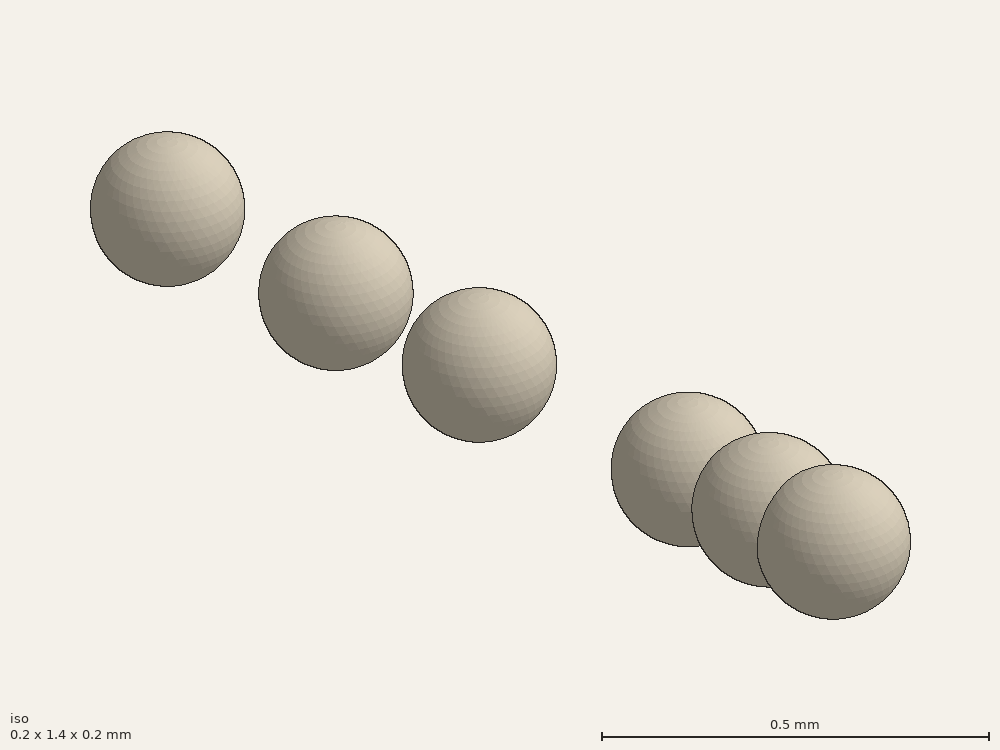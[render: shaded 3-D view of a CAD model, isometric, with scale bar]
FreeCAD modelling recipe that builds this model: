
FCSTD DOCUMENT  (FreeCAD 0.18R14555 (Git shallow))
Label: SIN_COS_TAN
License: All rights reserved
LicenseURL: http://en.wikipedia.org/wiki/All_rights_reserved
objects: Part::Feature×27, App::DocumentObjectGroupPython×7, Part::MultiFuse×6, Part::Part2DObjectPython×5, Part::Compound×4, Sketcher::SketchObject×1, PartDesign::Body×1, Part::Sphere×1
note: 45 computed .brp shape members not serialized (recipe doc carries the construction recipe); baked Part::Feature solids carry a one-line shape summary decoded from their .brp

FEATURE [Sketcher::SketchObject] Sketch
  MapMode = 5
  Support = -> [XY_Plane]
  sketch-geometry (17):
    g0: LineSegment StartX=0 StartY=1 StartZ=0 EndX=0 EndY=0 EndZ=0
    g1: LineSegment StartX=0 StartY=0 StartZ=0 EndX=0.523599 EndY=0 EndZ=0
    g2: LineSegment StartX=0.523599 StartY=0 StartZ=0 EndX=0.523599 EndY=0.5 EndZ=0
    g3: LineSegment StartX=0.523599 StartY=0 StartZ=0 EndX=0.785398 EndY=0 EndZ=0
    g4: LineSegment StartX=0.785398 StartY=0 StartZ=0 EndX=0.785398 EndY=0.705 EndZ=0
    g5: LineSegment StartX=0.785398 StartY=0 StartZ=0 EndX=1.0472 EndY=0 EndZ=0
    g6: LineSegment StartX=1.0472 StartY=0 StartZ=0 EndX=1.0472 EndY=0.865 EndZ=0
    g7: LineSegment StartX=1.0472 StartY=0 StartZ=0 EndX=1.5708 EndY=0 EndZ=0
    g8: LineSegment StartX=1.5708 StartY=0 StartZ=0 EndX=1.5708 EndY=1 EndZ=0
    g9: LineSegment StartX=0.523599 StartY=0.5 StartZ=0 EndX=0.523599 EndY=0.58 EndZ=0
    g10: LineSegment StartX=0.785398 StartY=0 StartZ=0 EndX=0.785398 EndY=1 EndZ=0
    g11: LineSegment StartX=1.0472 StartY=0.865 StartZ=0 EndX=1.0472 EndY=1.73205 EndZ=0
    g12: LineSegment StartX=1.39626 StartY=0 StartZ=0 EndX=1.39626 EndY=5.67 EndZ=0
    g13: LineSegment StartX=0.785398 StartY=0 StartZ=0 EndX=0.785398 EndY=1.41421 EndZ=0
    g14: LineSegment StartX=1.0472 StartY=0 StartZ=0 EndX=1.0472 EndY=1.1547 EndZ=0
    g15: LineSegment StartX=0.523599 StartY=0 StartZ=0 EndX=0.523599 EndY=2 EndZ=0
    g16: LineSegment StartX=0.174533 StartY=0 StartZ=0 EndX=0.174533 EndY=5.75 EndZ=0
  constraints (53):
    c: PointOnObject(g0,g-2)
    c: Coincident(g0,g-1)
    c: Coincident(g0,g1)
    c: PointOnObject(g1,g-1)
    c: Coincident(g1,g2)
    c: Vertical(g2)
    c: DistanceY(g0,g0) = 1
    c: DistanceY(g2,g2) = 0.5
    c: DistanceX(g1,g1) = 0.523599
    c: Coincident(g3,g4)
    c: Vertical(g4)
    c: PointOnObject(g3,g-1)
    c: Coincident(g1,g3)
    c: DistanceY(g4,g4) = 0.705
    c: DistanceX(g3,g3) = 0.261799
    c: Coincident(g3,g5)
    c: PointOnObject(g5,g-1)
    c: Coincident(g5,g6)
    c: Vertical(g6)
    c: Equal(g3,g5)
    c: DistanceY(g6,g6) = 0.865
    c: Coincident(g5,g7)
    c: PointOnObject(g7,g-1)
    c: Coincident(g7,g8)
    c: Vertical(g8)
    c: Equal(g0,g8)
    c: Equal(g1,g7)
    c: Coincident(g9,g2)
    c: Vertical(g9)
    c: DistanceY(g1,g9) = 0.58
    c: Coincident(g10,g3)
    c: Vertical(g10)
    c: Equal(g0,g10)
    c: Coincident(g11,g6)
    c: Vertical(g11)
    c: DistanceY(g5,g11) = 1.73205
    c: Vertical(g12)
    c: DistanceY(g12,g12) = 5.67
    c: PointOnObject(g12,g-1)
    c: DistanceX(g0,g12) = 1.39626
    c: Coincident(g13,g3)
    c: Vertical(g13)
    c: DistanceY(g13,g13) = 1.41421
    c: Coincident(g14,g5)
    c: Vertical(g14)
    c: DistanceY(g14,g14) = 1.1547
    c: Coincident(g15,g1)
    c: Vertical(g15)
    c: DistanceY(g15,g15) = 2
    c: PointOnObject(g16,g1)
    c: Vertical(g16)
    c: DistanceY(g16,g16) = 5.75
    c: DistanceX(g0,g16) = 0.174533
FEATURE [PartDesign::Body] Body
  Group = -> [Sketch]
  Origin = -> Origin
FEATURE [Part::Part2DObjectPython] BSpline  # Draft 2D object (typed FeaturePython)
  Closed = false
  MakeFace = true
  Parameterization = 1
  Points = (5) [(0,0,0),(0.523599,0.5,0),(0.785398,0.705,0),(1.0472,0.865,0),(1.5708,1,0)]
FEATURE [Part::Part2DObjectPython] BSpline001  # Draft 2D object (typed FeaturePython)
  Closed = false
  MakeFace = true
  Parameterization = 1
  Points = (3) [(0,0,0),(0.523599,0.58,0),(0.785398,1,0)]
FEATURE [Part::Part2DObjectPython] BezCurve  # Draft 2D object (typed FeaturePython)
  Closed = false
  Degree = 2
  MakeFace = true
  Points = (3) [(0.785398,0.996643,0),(1.31126,1.73713,0),(1.39626,5.67,0)]
FEATURE [Part::MultiFuse] Fusion  label="Tan"
  Shapes = -> [BSpline001,BezCurve]
FEATURE [Part::Feature] BSpline002
  Placement = pos=(3.14159,0,0) rot=(0,1,0;3.14159rad)
  shape: bbox 1.571 x 1 x 2e-07 mm, 0 faces, 0 solids (baked)
FEATURE [Part::Feature] BSpline003
  Placement = pos=(3.14,0,0) rot=(1,0,0;3.14159rad)
  shape: bbox 1.571 x 1 x 2e-07 mm, 0 faces, 0 solids (baked)
FEATURE [Part::Feature] BSpline002001  label="BSpline004"
  Placement = pos=(6.28159,0,0) rot=(0,0,1;3.14159rad)
  shape: bbox 1.571 x 1 x 2e-07 mm, 0 faces, 0 solids (baked)
FEATURE [Part::MultiFuse] Fusion001
  Shapes = -> [BSpline003,BSpline002001]
FEATURE [Part::Feature] Fusion001001  label="Fusion002"
  Placement = pos=(-1.57,0,0) rot=(0,0,1;0rad)
  shape: bbox 3.142 x 1 x 2e-07 mm, 0 faces, 0 solids (baked)
FEATURE [Part::Feature] BSpline002002  label="BSpline005"
  Placement = pos=(1.57159,0,0) rot=(0,1,0;3.14159rad)
  shape: bbox 1.571 x 1 x 2e-07 mm, 0 faces, 0 solids (baked)
FEATURE [Part::Feature] BSpline002003  label="BSpline006"
  Placement = pos=(4.71,0,0) rot=(0,0,1;0rad)
  shape: bbox 1.571 x 1 x 2e-07 mm, 0 faces, 0 solids (baked)
FEATURE [Part::MultiFuse] Fusion001002  label="Sine"
  Shapes = -> [BSpline002,BSpline,Fusion001]
FEATURE [Part::MultiFuse] Fusion001003  label="Cosine"
  Shapes = -> [Fusion001001,BSpline002002,BSpline002003]
FEATURE [Part::Feature] Fusion001004  label="Tan001"
  Placement = pos=(3.14,0,0) rot=(0,0,1;0rad)
  shape: bbox 1.396 x 5.67 x 2e-07 mm, 0 faces, 0 solids (baked)
FEATURE [Part::Feature] Fusion001004001  label="Tan002"
  Placement = pos=(3.14,0,0) rot=(0,0,1;3.14159rad)
  shape: bbox 1.396 x 5.67 x 2e-07 mm, 0 faces, 0 solids (baked)
FEATURE [Part::Feature] Fusion001004001001  label="Tan003"
  Placement = pos=(6.28,0,0) rot=(0,0,1;3.14159rad)
  shape: bbox 1.396 x 5.67 x 2e-07 mm, 0 faces, 0 solids (baked)
FEATURE [Part::Compound] Compound  label="Tangent"
  Links = -> [Fusion001004,Fusion001004001,Fusion001004001001,Fusion]
FEATURE [Part::Part2DObjectPython] BSpline002004  # Draft 2D object (typed FeaturePython)
  Closed = false
  MakeFace = true
  Parameterization = 1
  Points = (3) [(1.5708,1,1.22465e-16),(1.0472,1.1563,0),(0.785398,1.41054,0)]
FEATURE [Part::Part2DObjectPython] BezCurve001  # Draft 2D object (typed FeaturePython)
  Closed = false
  Degree = 2
  MakeFace = true
  Points = (3) [(0.785398,1.41421,0),(0.258646,2.00333,0),(0.174533,5.74801,0)]
FEATURE [Part::MultiFuse] Fusion001004001002
  Shapes = -> [BSpline002004,BezCurve001]
FEATURE [Part::Feature] Fusion001004001002001  label="Fusion001004001003"
  Placement = pos=(3.14,0,0) rot=(0,1,0;3.14159rad)
  shape: bbox 1.396 x 4.748 x 2e-07 mm, 0 faces, 0 solids (baked)
FEATURE [Part::MultiFuse] Fusion001004001002002
  Shapes = -> [Fusion001004001002,Fusion001004001002001]
FEATURE [Part::Feature] Fusion001004001002002001  label="Fusion001004001002003"
  Placement = pos=(3.14,0,0) rot=(1,0,0;3.14159rad)
  shape: bbox 2.791 x 4.748 x 2e-07 mm, 0 faces, 0 solids (baked)
FEATURE [Part::Compound] Compound001  label="Cosecant"
  Links = -> [Fusion001004001002002,Fusion001004001002002001]
FEATURE [Part::Feature] Fusion001004001002001001  label="Fusion001004001002004"
  Placement = pos=(1.57,0,0) rot=(0,1,0;3.14159rad)
  shape: bbox 1.396 x 4.748 x 2e-07 mm, 0 faces, 0 solids (baked)
FEATURE [Part::Feature] Fusion001004001002001001001  label="Fusion001004001002005"
  Placement = pos=(4.71,0,0) rot=(0,0,1;0rad)
  shape: bbox 1.396 x 4.748 x 2e-07 mm, 0 faces, 0 solids (baked)
FEATURE [Part::Feature] Fusion001004001002002001001  label="Fusion001004001002006"
  Placement = pos=(1.57,0,0) rot=(1,0,0;3.14159rad)
  shape: bbox 2.791 x 4.748 x 2e-07 mm, 0 faces, 0 solids (baked)
FEATURE [Part::Compound] Compound002  label="Secant"
  Links = -> [Fusion001004001002001001,Fusion001004001002001001001,Fusion001004001002002001001]
FEATURE [Part::Feature] Edge
  Placement = pos=(3.14,0,3e-15) rot=(0,1,0;3.14159rad)
  shape: bbox 0.6109 x 4.673 x 2e-07 mm, 0 faces, 0 solids (baked)
FEATURE [Part::Feature] Edge001
  Placement = pos=(3.14,0,3e-15) rot=(0,1,0;3.14159rad)
  shape: bbox 0.7854 x 1 x 2e-07 mm, 0 faces, 0 solids (baked)
FEATURE [Part::Feature] Edge002
  Placement = pos=(3.14,0,3e-15) rot=(1,0,0;3.14159rad)
  shape: bbox 0.6109 x 4.673 x 2e-07 mm, 0 faces, 0 solids (baked)
FEATURE [Part::Feature] Edge003
  Placement = pos=(3.14,0,3e-15) rot=(1,0,0;3.14159rad)
  shape: bbox 0.7854 x 1 x 2e-07 mm, 0 faces, 0 solids (baked)
FEATURE [Part::Feature] Edge004
  Placement = pos=(6.28,0,3e-15) rot=(1,0,0;3.14159rad)
  shape: bbox 0.6109 x 4.673 x 2e-07 mm, 0 faces, 0 solids (baked)
FEATURE [Part::Feature] Edge005
  Placement = pos=(6.28,0,3e-15) rot=(1,0,0;3.14159rad)
  shape: bbox 0.7854 x 1 x 2e-07 mm, 0 faces, 0 solids (baked)
FEATURE [Part::Feature] Edge006
  Placement = pos=(6.28,0,3e-15) rot=(0,1,0;3.14159rad)
  shape: bbox 0.6109 x 4.673 x 2e-07 mm, 0 faces, 0 solids (baked)
FEATURE [Part::Feature] Edge007
  Placement = pos=(6.28,0,3e-15) rot=(0,1,0;3.14159rad)
  shape: bbox 0.7854 x 1 x 2e-07 mm, 0 faces, 0 solids (baked)
FEATURE [Part::Compound] Compound003  label="Cotangent"
  Links = -> [Edge,Edge007,Edge002,Edge004,Edge003,Edge001,Edge005,Edge006]
  Placement = pos=(-1.5708,0,0) rot=(0,0,1;0rad)
FEATURE [Part::Sphere] Sphere  label="sin"
  Angle1 = -90
  Angle2 = 90
  Angle3 = 360
  AttacherType = Attacher::AttachEngine3D
  Placement = pos=(0.973894,0.827081,0) rot=(0,0,1;0rad)
  Radius = 0.1
FEATURE [Part::Feature] Sphere001  label="cos"
  Placement = pos=(0.973894,0.562083,0) rot=(0,0,1;0rad)
  shape: bbox 0.2 x 0.2 x 0.2 mm, 1 faces (baked)
FEATURE [Part::Feature] Sphere002  label="tan"
  Placement = pos=(0.973894,1.47146,0) rot=(0,0,1;0rad)
  shape: bbox 0.2 x 0.2 x 0.2 mm, 1 faces (baked)
FEATURE [Part::Feature] Sphere003  label="cosec"
  Placement = pos=(0.973894,1.20907,0) rot=(0,0,1;0rad)
  shape: bbox 0.2 x 0.2 x 0.2 mm, 1 faces (baked)
FEATURE [Part::Feature] Sphere004  label="sec"
  Placement = pos=(0.973894,1.7791,0) rot=(0,0,1;0rad)
  shape: bbox 0.2 x 0.2 x 0.2 mm, 1 faces (baked)
FEATURE [Part::Feature] Sphere005  label="cotg"
  Placement = pos=(0.973894,0.679599,0) rot=(0,0,1;0rad)
  shape: bbox 0.2 x 0.2 x 0.2 mm, 1 faces (baked)
FEATURE [App::DocumentObjectGroupPython] My_Placer  label="sin001"  # scripted group (container) (typed FeaturePython)
  Placement = pos=(0.973894,0.827081,0) rot=(0,0,1;0rad)
  RotAxis = (0,0,1)
  RotCenter = (0,0,0)
  arc = 0
  arc0 = 0
  arc1 = 90
  target = -> Sphere
  time = 0.62
  x = x0
  x0 = 0.973894
  x1 = 200
  y = y0
  y0 = 0.827081
  y1 = 0
  z = 0
  z0 = 0
  z1 = 0
  expr: y0 = sin(time * 90)
  expr: x0 = time * pi / 2
FEATURE [App::DocumentObjectGroupPython] My_Placer001  label="cos001"  # scripted group (container) (typed FeaturePython)
  Placement = pos=(0.973894,0.562083,0) rot=(0,0,1;0rad)
  RotAxis = (0,0,1)
  RotCenter = (0,0,0)
  arc = 0
  arc0 = 0
  arc1 = 90
  target = -> Sphere001
  time = 0.62
  x = x0
  x0 = 0.973894
  x1 = 200
  y = y0
  y0 = 0.562083
  y1 = 0
  z = 0
  z0 = 0
  z1 = 0
  expr: y0 = cos(time * 90)
  expr: x0 = time * pi / 2
FEATURE [App::DocumentObjectGroupPython] My_Placer002  label="tan001"  # scripted group (container) (typed FeaturePython)
  Placement = pos=(0.973894,1.47146,0) rot=(0,0,1;0rad)
  RotAxis = (0,0,1)
  RotCenter = (0,0,0)
  arc = 0
  arc0 = 0
  arc1 = 90
  target = -> Sphere002
  time = 0.62
  x = x0
  x0 = 0.973894
  x1 = 200
  y = y0
  y0 = 1.47146
  y1 = 0
  z = 0
  z0 = 0
  z1 = 0
  expr: y0 = tan(time * 90)
  expr: x0 = time * pi / 2
FEATURE [App::DocumentObjectGroupPython] My_Placer003  label="cosec001"  # scripted group (container) (typed FeaturePython)
  Placement = pos=(0.973894,1.20907,0) rot=(0,0,1;0rad)
  RotAxis = (0,0,1)
  RotCenter = (0,0,0)
  arc = 0
  arc0 = 0
  arc1 = 90
  target = -> Sphere003
  time = 0.62
  x = x0
  x0 = 0.973894
  x1 = 200
  y = 1/y0
  y0 = 0.827081
  y1 = 0
  z = 0
  z0 = 0
  z1 = 0
  expr: y0 = sin(time * 90)
  expr: x0 = time * pi / 2
FEATURE [App::DocumentObjectGroupPython] My_Placer004  label="sec001"  # scripted group (container) (typed FeaturePython)
  Placement = pos=(0.973894,1.7791,0) rot=(0,0,1;0rad)
  RotAxis = (0,0,1)
  RotCenter = (0,0,0)
  arc = 0
  arc0 = 0
  arc1 = 90
  target = -> Sphere004
  time = 0.62
  x = x0
  x0 = 0.973894
  x1 = 200
  y = 1/y0
  y0 = 0.562083
  y1 = 0
  z = 0
  z0 = 0
  z1 = 0
  expr: y0 = cos(time * 90)
  expr: x0 = time * pi / 2
FEATURE [App::DocumentObjectGroupPython] My_Placer005  label="cotg001"  # scripted group (container) (typed FeaturePython)
  Placement = pos=(0.973894,0.679599,0) rot=(0,0,1;0rad)
  RotAxis = (0,0,1)
  RotCenter = (0,0,0)
  arc = 0
  arc0 = 0
  arc1 = 90
  target = -> Sphere005
  time = 0.62
  x = x0
  x0 = 0.973894
  x1 = 200
  y = 1/y0
  y0 = 1.47146
  y1 = 0
  z = 0
  z0 = 0
  z1 = 0
  expr: y0 = tan(time * 90)
  expr: x0 = time * pi / 2
FEATURE [App::DocumentObjectGroupPython] My_Manager  # scripted group (container) (typed FeaturePython)
  Group = -> [My_Placer,My_Placer001,My_Placer002,My_Placer003,My_Placer004,My_Placer005]
  intervall = 400
  sleeptime = 0.02
  start = 0
  step = 62
  text = NO
